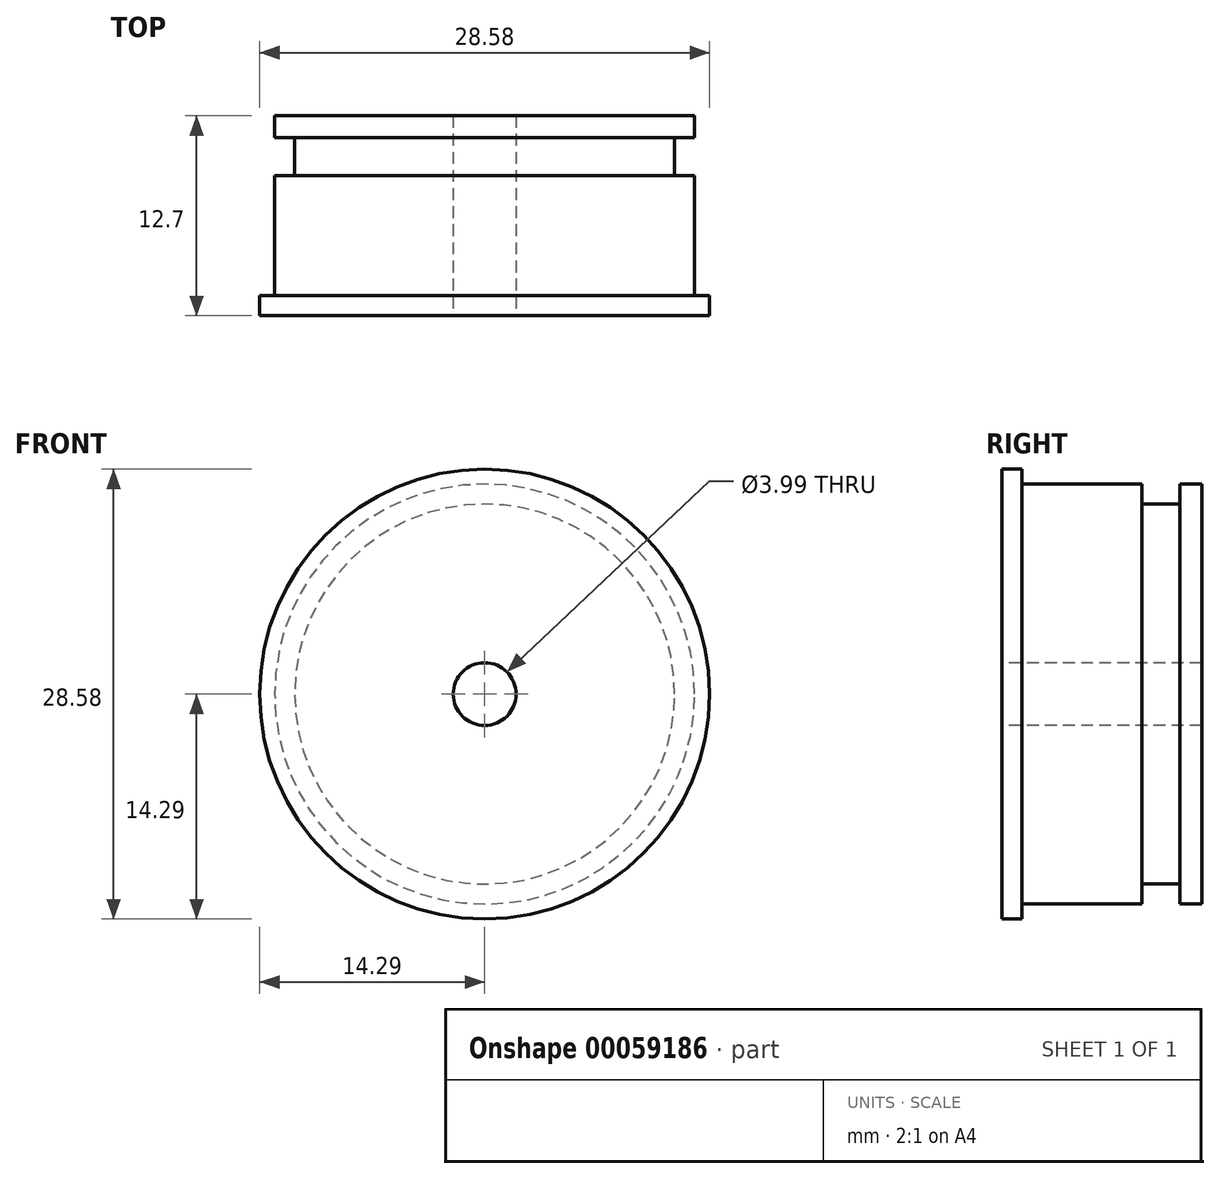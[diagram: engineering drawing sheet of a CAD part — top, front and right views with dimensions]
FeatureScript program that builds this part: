
annotation { "Feature Type Name" : "Feature", "Feature Type Description" : "" }
export const myFeature = defineFeature(function(context is Context, id is Id, definition is map)
    precondition{}
    {
        {
            var Q0;
            Q0=qCreatedBy(makeId("Top.planeOp"),FACE);
            var sketch = newSketch(context, id + "F0", { "sketchPlane" : qUnion([Q0])});
            skLineSegment(sketch, "E0", {"start": v(0, 0) * mm, "end": v(0, 12.7) * mm});
            skLineSegment(sketch, "E1", {"start": v(0, 12.7) * mm, "end": v(13.34, 12.7) * mm});
            skLineSegment(sketch, "E2", {"start": v(13.34, 12.7) * mm, "end": v(13.34, 11.3) * mm});
            skLineSegment(sketch, "E3", {"start": v(13.34, 11.3) * mm, "end": v(12.07, 11.3) * mm});
            skLineSegment(sketch, "E4", {"start": v(12.07, 11.3) * mm, "end": v(12.07, 8.89) * mm});
            skLineSegment(sketch, "E5", {"start": v(12.07, 8.9) * mm, "end": v(13.33, 8.9) * mm});
            skLineSegment(sketch, "E6", {"start": v(13.34, 8.9) * mm, "end": v(13.34, 1.27) * mm});
            skLineSegment(sketch, "E7", {"start": v(13.34, 1.27) * mm, "end": v(14.29, 1.27) * mm});
            skLineSegment(sketch, "E8", {"start": v(14.29, 1.27) * mm, "end": v(14.29, 0) * mm});
            skLineSegment(sketch, "E9", {"start": v(14.29, 0) * mm, "end": v(0, 0) * mm});
            skSolve(sketch);
        }
        {
            var Q0;
            Q0=makeQuery(id+"F0.imprint","IMPRINT",FACE,{"disambiguationData":[TD([[makeQuery(id+"F0.imprint","IMPRINT",EDGE,{"derivedFrom":sQuery(id+"F0.wireOp",EDGE,"E0")}),-1.0]])]});
            var Q1;
            Q1=sQuery(id+"F0.wireOp",EDGE,"E0");
            revolve(context, id + "F1", {"entities" : qUnion([Q0]), "axis" : qUnion([Q1]), "revolveType" : RevolveType.FULL});
        }
        {
            var Q0;
            Q0=makeQuery(id+"F1.opRevolve","SWEPT_FACE",FACE,{"disambiguationData":[OSD([sQuery(id+"F0.wireOp",EDGE,"E9")])]});
            var sketch = newSketch(context, id + "F2", { "sketchPlane" : qUnion([Q0])});
            skPoint(sketch, "E10", {"position": v(0, 0) * mm});
            skSolve(sketch);
        }
        {
            var Q0;
            Q0=sQuery(id+"F2.wireOp",VERTEX,"E10");
            var Q1;
            Q1=makeQuery(id+"F1.opRevolve","SWEPT_BODY",BODY,{"disambiguationData":[OSD([sQuery(id+"F0.wireOp",EDGE,"E0"),sQuery(id+"F0.wireOp",EDGE,"E1"),sQuery(id+"F0.wireOp",EDGE,"E2"),sQuery(id+"F0.wireOp",EDGE,"E3"),sQuery(id+"F0.wireOp",EDGE,"E4"),sQuery(id+"F0.wireOp",EDGE,"E5"),sQuery(id+"F0.wireOp",EDGE,"E6"),sQuery(id+"F0.wireOp",EDGE,"E7"),sQuery(id+"F0.wireOp",EDGE,"E8"),sQuery(id+"F0.wireOp",EDGE,"E9")])]});
            hole(context, id + "F3", {"style" : HoleStyle.SIMPLE, "holeDiameter" : 4 * mm, "endStyle" : HoleEndStyle.THROUGH, "locations" : qUnion([Q0]), "scope" : qUnion([Q1]), "isTappedThrough" : true});
        }
    });
